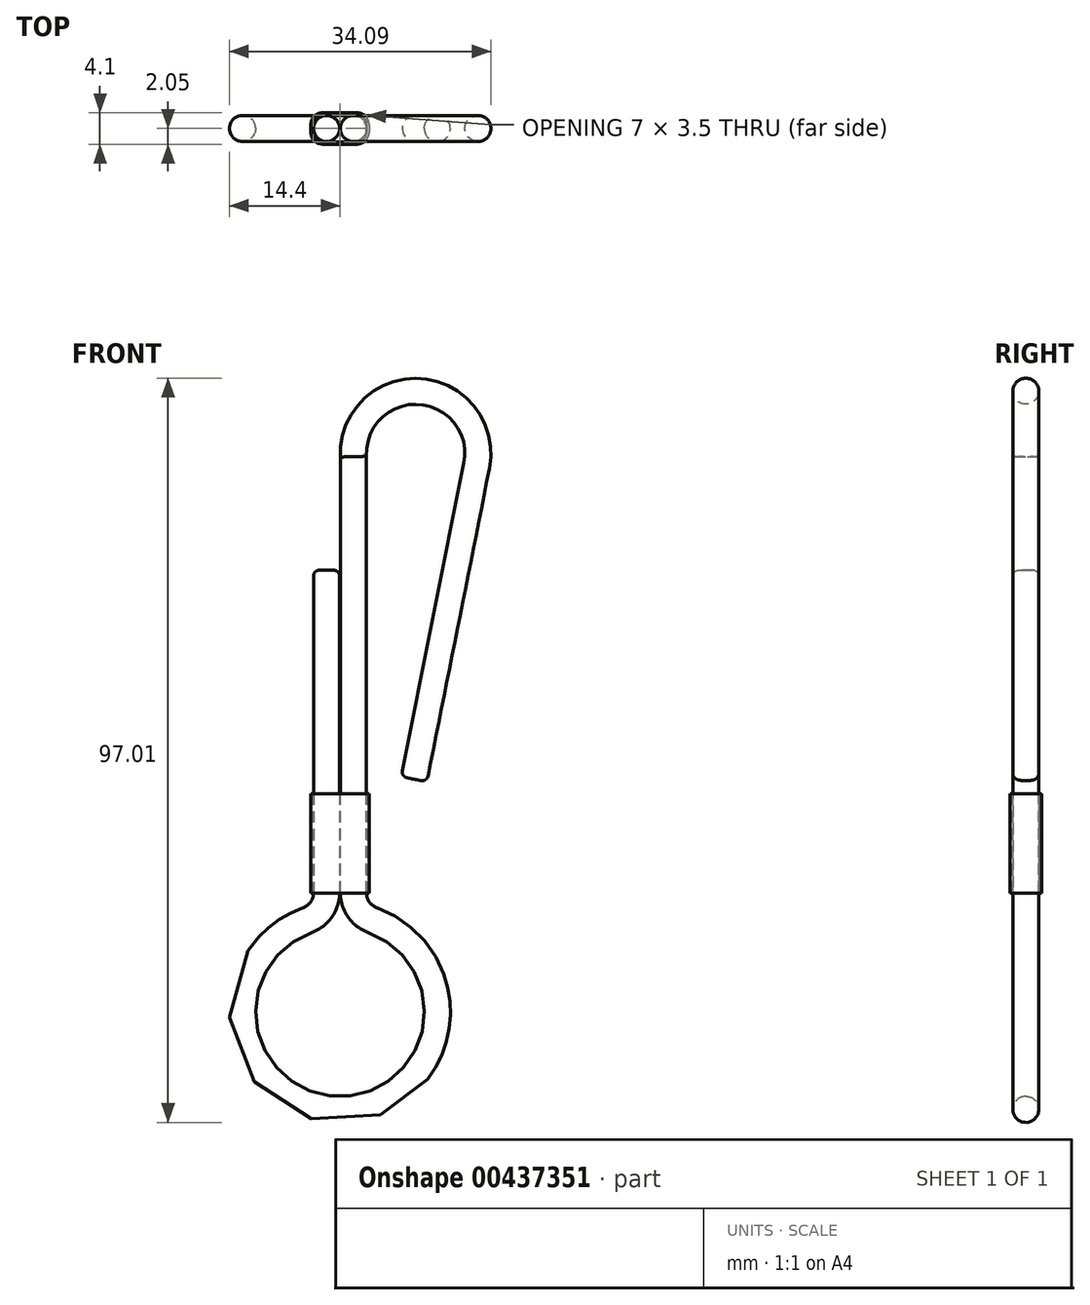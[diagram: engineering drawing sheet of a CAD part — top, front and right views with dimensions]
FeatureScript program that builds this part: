
annotation { "Feature Type Name" : "Feature", "Feature Type Description" : "" }
export const myFeature = defineFeature(function(context is Context, id is Id, definition is map)
    precondition{}
    {
        {
            var Q0;
            Q0=qCreatedBy(makeId("Front.planeOp"),FACE);
            var sketch = newSketch(context, id + "F0", { "sketchPlane" : qUnion([Q0])});
            skCircle(sketch, "E0", {"center": v(0, 0) * mm, "radius": 12.7 * mm});
            skLineSegment(sketch, "E1.bottom", {"start": v(-3.5, 28.92) * mm, "end": v(3.5, 28.92) * mm, "construction": true});
            skLineSegment(sketch, "E1.top", {"start": v(-3.5, 24.04) * mm, "end": v(3.5, 24.04) * mm, "construction": true});
            skLineSegment(sketch, "E1.left", {"start": v(-3.5, 28.92) * mm, "end": v(-3.5, 24.04) * mm, "construction": true});
            skLineSegment(sketch, "E1.right", {"start": v(3.5, 28.92) * mm, "end": v(3.5, 24.04) * mm, "construction": true});
            skPoint(sketch, "E1.middle", {"position": v(0, 26.48) * mm});
            skLineSegment(sketch, "E2", {"start": v(-3.5, 28.92) * mm, "end": v(0, 24.04) * mm, "construction": true});
            skLineSegment(sketch, "E3", {"start": v(0, 24.04) * mm, "end": v(0, 28.92) * mm, "construction": true});
            skLineSegment(sketch, "E4", {"start": v(0, 28.92) * mm, "end": v(-3.5, 24.04) * mm, "construction": true});
            skLineSegment(sketch, "E5", {"start": v(-1.75, 57.58) * mm, "end": v(-1.75, 12.58) * mm});
            skPoint(sketch, "E5.startSnap0", {"position": v(-1.75, 26.48) * mm});
            skLineSegment(sketch, "E6", {"start": v(3.5, 24.04) * mm, "end": v(0, 28.92) * mm, "construction": true});
            skLineSegment(sketch, "E7", {"start": v(3.5, 28.92) * mm, "end": v(0, 24.04) * mm, "construction": true});
            skLineSegment(sketch, "E8", {"start": v(1.75, 12.58) * mm, "end": v(1.75, 72.58) * mm});
            skPoint(sketch, "E8.startSnap0", {"position": v(1.75, 26.48) * mm});
            skCircle(sketch, "E9", {"center": v(9.87, 72.79) * mm, "radius": 8.12 * mm});
            skPoint(sketch, "E9.second.point", {"position": v(17.99, 72.58) * mm});
            skPoint(sketch, "E9.third.point", {"position": v(13.8, 79.9) * mm});
            skLineSegment(sketch, "E10", {"start": v(9.65, 30.34) * mm, "end": v(17.83, 71.2) * mm});
            skSolve(sketch);
        }
        {
            var Q0;
            Q0=qCreatedBy(makeId("Front.planeOp"),FACE);
            var sketch = newSketch(context, id + "F1", { "sketchPlane" : qUnion([Q0])});
            skLineSegment(sketch, "E11.0", {"start": v(-1.75, 57.58) * mm, "end": v(-1.75, 15.55) * mm});
            skArc(sketch, "E12.0.0", {"start": v(-4.28, 11.96) * mm, "mid": v(0, -12.7) * mm, "end": v(4.28, 11.96) * mm});
            skLineSegment(sketch, "E13.0", {"start": v(1.75, 15.55) * mm, "end": v(1.75, 72.58) * mm});
            skArc(sketch, "E14.0", {"start": v(17.83, 71.2) * mm, "mid": v(10.57, 80.88) * mm, "end": v(1.75, 72.58) * mm});
            skLineSegment(sketch, "E15.0", {"start": v(9.65, 30.34) * mm, "end": v(17.83, 71.2) * mm});
            skPoint(sketch, "E16.visualSharp", {"position": v(-1.75, 12.58) * mm});
            skArc(sketch, "E16.filletArc", {"start": v(-4.28, 11.96) * mm, "mid": v(-2.45, 13.35) * mm, "end": v(-1.75, 15.55) * mm});
            skPoint(sketch, "E17.visualSharp", {"position": v(1.75, 12.58) * mm});
            skArc(sketch, "E17.filletArc", {"start": v(1.75, 15.55) * mm, "mid": v(2.45, 13.35) * mm, "end": v(4.28, 11.96) * mm});
            skSolve(sketch);
        }
        {
            var Q0;
            Q0=qCreatedBy(makeId("Top.planeOp"),FACE);
            var Q1;
            Q1=sQuery(id+"F1.wireOp",VERTEX,"E11.0.start");
            cPlane(context, id + "F2", {"entities" : qUnion([Q0, Q1]), "cplaneType" : CPlaneType.PLANE_POINT, "offset" : 25.4 * mm, "width" : 152.4 * mm, "height" : 152.4 * mm});
        }
        {
            var Q0;
            Q0=qCreatedBy(id+"F2.planeOp",FACE);
            var sketch = newSketch(context, id + "F3", { "sketchPlane" : qUnion([Q0])});
            skCircle(sketch, "E18", {"center": v(-1.75, 0) * mm, "radius": 1.7 * mm});
            skSolve(sketch);
        }
        {
            var Q0;
            Q0=makeQuery(id+"F3.imprint","IMPRINT",FACE,{"disambiguationData":[TD([[makeQuery(id+"F3.imprint","IMPRINT",EDGE,{"derivedFrom":sQuery(id+"F3.wireOp",EDGE,"E18")}),1.0]])]});
            var Q1;
            Q1=sQuery(id+"F1.wireOp",EDGE,"E11.0");
            var Q2;
            Q2=sQuery(id+"F1.wireOp",EDGE,"E16.filletArc");
            var Q3;
            Q3=sQuery(id+"F1.wireOp",EDGE,"E12.0.0");
            var Q4;
            Q4=sQuery(id+"F1.wireOp",EDGE,"E17.filletArc");
            var Q5;
            Q5=sQuery(id+"F1.wireOp",EDGE,"E13.0");
            var Q6;
            Q6=sQuery(id+"F1.wireOp",EDGE,"E14.0");
            var Q7;
            Q7=sQuery(id+"F1.wireOp",EDGE,"E15.0");
            sweep(context, id + "F4", {"profiles" : qUnion([Q0]), "path" : qUnion([Q1, Q2, Q3, Q4, Q5, Q6, Q7])});
        }
        {
            var Q0;
            Q0=makeQuery(id+"F4.opSweep","CAP_EDGE",EDGE,{"disambiguationData":[OSD([sQuery(id+"F1.wireOp",VERTEX,"E11.0.start"),sQuery(id+"F3.wireOp",EDGE,"E18")])],"isStart":true});
            var Q1;
            Q1=makeQuery(id+"F4.opSweep","CAP_EDGE",EDGE,{"disambiguationData":[OSD([sQuery(id+"F1.wireOp",VERTEX,"E15.0.start"),sQuery(id+"F3.wireOp",EDGE,"E18")])],"isStart":false});
            fillet(context, id + "F5", {"entities" : qUnion([Q0, Q1]), "radius" : 0.76 * mm, "tangentPropagation" : true, "allowEdgeOverflow" : false});
        }
        {
            var Q0;
            Q0=qCreatedBy(makeId("Top.planeOp"),FACE);
            cPlane(context, id + "F6", {"entities" : qUnion([Q0]), "cplaneType" : CPlaneType.OFFSET, "offset" : 15.47 * mm, "width" : 152.4 * mm, "height" : 152.4 * mm});
        }
        {
            var Q0;
            Q0=qCreatedBy(id+"F6.planeOp",FACE);
            var sketch = newSketch(context, id + "F7", { "sketchPlane" : qUnion([Q0])});
            skLineSegment(sketch, "E19.bottom", {"start": v(-2.23, 1.75) * mm, "end": v(2.23, 1.75) * mm});
            skLineSegment(sketch, "E19.top", {"start": v(-2.23, -1.75) * mm, "end": v(2.23, -1.75) * mm});
            skLineSegment(sketch, "E19.left", {"start": v(-3.5, 0.48) * mm, "end": v(-3.5, -0.48) * mm});
            skLineSegment(sketch, "E19.right", {"start": v(3.5, 0.48) * mm, "end": v(3.5, -0.48) * mm});
            skPoint(sketch, "E19.middle", {"position": v(0, 0) * mm});
            skPoint(sketch, "E20.visualSharp", {"position": v(-3.5, 1.75) * mm});
            skArc(sketch, "E20.filletArc", {"start": v(-2.23, 1.75) * mm, "mid": v(-3.13, 1.38) * mm, "end": v(-3.5, 0.48) * mm});
            skPoint(sketch, "E21.visualSharp", {"position": v(-3.5, -1.75) * mm});
            skArc(sketch, "E21.filletArc", {"start": v(-3.5, -0.48) * mm, "mid": v(-3.13, -1.38) * mm, "end": v(-2.23, -1.75) * mm});
            skPoint(sketch, "E22.visualSharp", {"position": v(3.5, 1.75) * mm});
            skArc(sketch, "E22.filletArc", {"start": v(3.5, 0.48) * mm, "mid": v(3.13, 1.38) * mm, "end": v(2.23, 1.75) * mm});
            skPoint(sketch, "E23.visualSharp", {"position": v(3.5, -1.75) * mm});
            skArc(sketch, "E23.filletArc", {"start": v(2.23, -1.75) * mm, "mid": v(3.13, -1.38) * mm, "end": v(3.5, -0.48) * mm});
            skArc(sketch, "E24.0", {"start": v(-2.23, 2.05) * mm, "mid": v(-3.34, 1.6) * mm, "end": v(-3.8, 0.48) * mm});
            skLineSegment(sketch, "E24.1", {"start": v(-3.8, 0.48) * mm, "end": v(-3.8, -0.48) * mm});
            skLineSegment(sketch, "E24.2", {"start": v(-2.23, 2.05) * mm, "end": v(2.23, 2.05) * mm});
            skArc(sketch, "E24.3", {"start": v(-3.8, -0.48) * mm, "mid": v(-3.34, -1.6) * mm, "end": v(-2.23, -2.05) * mm});
            skArc(sketch, "E24.4", {"start": v(3.8, 0.48) * mm, "mid": v(3.34, 1.6) * mm, "end": v(2.23, 2.05) * mm});
            skLineSegment(sketch, "E24.5", {"start": v(3.8, 0.48) * mm, "end": v(3.8, -0.48) * mm});
            skArc(sketch, "E24.6", {"start": v(2.23, -2.05) * mm, "mid": v(3.34, -1.6) * mm, "end": v(3.8, -0.48) * mm});
            skLineSegment(sketch, "E24.7", {"start": v(-2.23, -2.05) * mm, "end": v(2.23, -2.05) * mm});
            skSolve(sketch);
        }
        {
            var Q0;
            Q0 = qSketchRegion(id + "F7", true);
            extrude(context, id + "F8", {"entities" : qUnion([Q0]), "depth" : 13 * mm});
        }
    });
